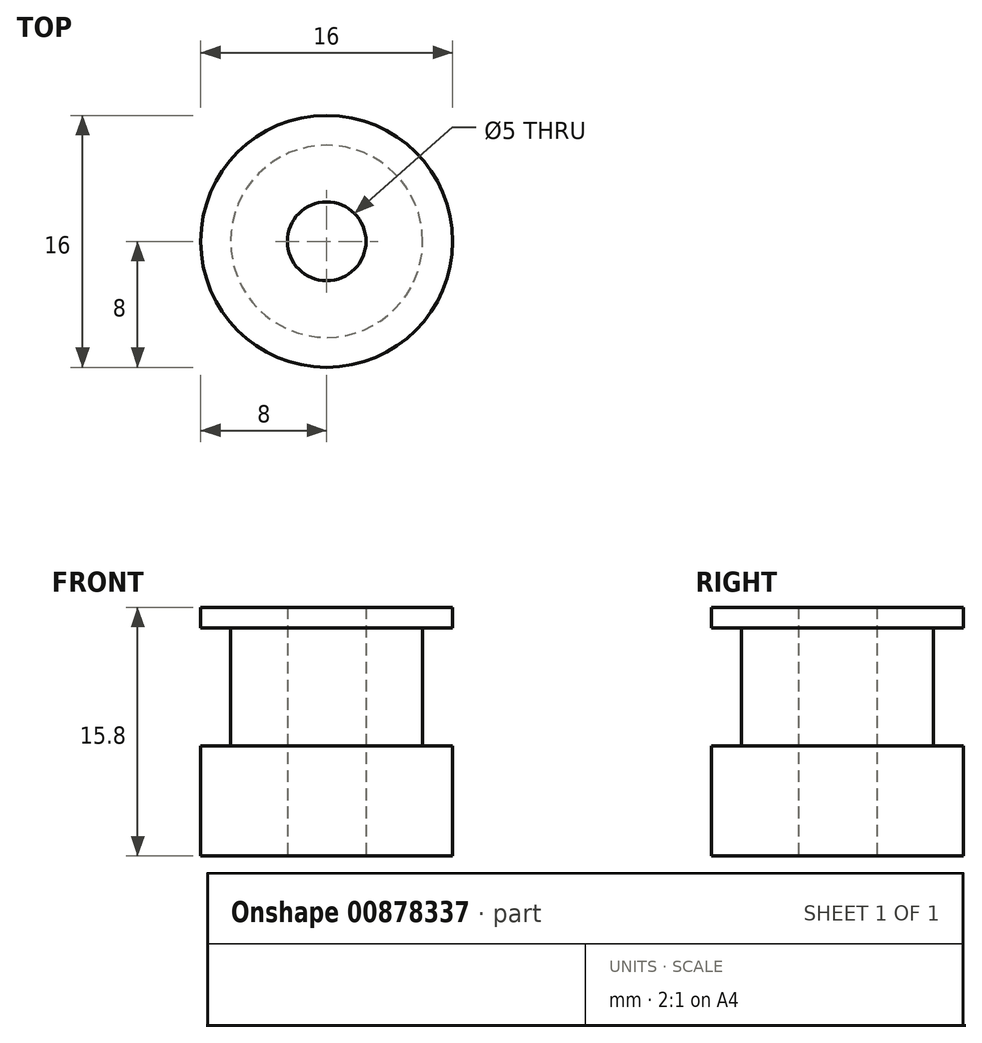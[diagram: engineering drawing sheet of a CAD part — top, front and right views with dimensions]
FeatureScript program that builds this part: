
annotation { "Feature Type Name" : "Feature", "Feature Type Description" : "" }
export const myFeature = defineFeature(function(context is Context, id is Id, definition is map)
    precondition{}
    {
        {
            var Q0;
            Q0=qCreatedBy(makeId("Top.planeOp"),FACE);
            var sketch = newSketch(context, id + "F0", { "sketchPlane" : qUnion([Q0])});
            skCircle(sketch, "E0", {"center": v(0, 0) * mm, "radius": 8 * mm});
            skCircle(sketch, "E1", {"center": v(0, 0) * mm, "radius": 2.5 * mm});
            skSolve(sketch);
        }
        {
            var Q0;
            Q0 = qSketchRegion(id + "F0", true);
            extrude(context, id + "F1", {"entities" : qUnion([Q0]), "depth" : 7 * mm, "offsetDistance" : 25 * mm});
        }
        {
            var Q0;
            Q0=makeQuery(id+"F1.opExtrude","CAP_FACE",FACE,{"disambiguationData":[OSD([sQuery(id+"F0.wireOp",EDGE,"E0"),sQuery(id+"F0.wireOp",EDGE,"E1")])],"isStart":false});
            var sketch = newSketch(context, id + "F2", { "sketchPlane" : qUnion([Q0])});
            skCircle(sketch, "E2", {"center": v(0, 0) * mm, "radius": 6.1 * mm});
            skCircle(sketch, "E3.0", {"center": v(0, 0) * mm, "radius": 2.5 * mm});
            skSolve(sketch);
        }
        {
            var Q0;
            Q0 = qSketchRegion(id + "F2", true);
            extrude(context, id + "F3", {"entities" : qUnion([Q0]), "operationType" : NewBodyOperationType.ADD, "depth" : 7.5 * mm, "offsetDistance" : 25 * mm});
        }
        {
            var Q0;
            Q0=makeQuery(id+"F3.opExtrude","CAP_FACE",FACE,{"disambiguationData":[OSD([sQuery(id+"F2.wireOp",EDGE,"E2"),sQuery(id+"F2.wireOp",EDGE,"E3.0")])],"isStart":false});
            var sketch = newSketch(context, id + "F4", { "sketchPlane" : qUnion([Q0])});
            skCircle(sketch, "E4", {"center": v(0, 0) * mm, "radius": 8 * mm});
            skCircle(sketch, "E5.0", {"center": v(0, 0) * mm, "radius": 2.5 * mm});
            skSolve(sketch);
        }
        {
            var Q0;
            Q0=makeQuery(id+"F4.imprint","IMPRINT",FACE,{"disambiguationData":[TD([[makeQuery(id+"F4.imprint","IMPRINT",EDGE,{"derivedFrom":sQuery(id+"F4.wireOp",EDGE,"E5.0")}),-1.0]])]});
            var Q1;
            Q1=makeQuery(id+"F4.imprint","IMPRINT",FACE,{"disambiguationData":[TD([[makeQuery(id+"F4.imprint","IMPRINT",EDGE,{"derivedFrom":sQuery(id+"F4.wireOp",EDGE,"E4")}),1.0]])]});
            extrude(context, id + "F5", {"entities" : qUnion([Q0, Q1]), "operationType" : NewBodyOperationType.ADD, "depth" : 1.3 * mm, "offsetDistance" : 25 * mm});
        }
    });
